# Revit family: F1120-C
name_source: partatom
category: Plumbing Fixtures
revit_build: Autodesk Revit 2018 (Build: 20170223_1515(x64)
units: mm (PartAtom-declared; Revit-internal decimal feet)

## family parameters
Cut with Voids When Loaded = No
Host = Face
Part Type = Normal
Room Calculation Point = No
Round Connector Dimension = Use Radius
Shared = No

## types (3) — shared parameters
Default Elevation = 0' - 0"
Description = FLOOR DRAIN WITH INTEGRAL DEEP SEAL TRAP
Floor Drain Material = Paint - Sherwin Williams Paint - #952C2A - Bellwood Red
Manufacturer = MIFAB
Model = F1120-C
URL = WWW.MIFAB.COM
zero-valued in all types: CWFU, WFU

## per-type parameters (varying)
| type | A | Adjustment | B | Free Area | Pipe Diameter | Pipe Radius | Top Diameter |
| F1120-C - Ø2" | 0' - 2 1/4" | 0' - 1 1/2" | 0' - 5 3/16" | 0' - 8" | 0' - 2" | 0' - 1" | 0' - 5" |
| F1120-C - Ø3" | 0' - 2 1/2" | 0' - 1 1/2" | 0' - 5 3/16" | 0' - 9" | 0' - 3" | 0' - 1 1/2" | 0' - 6" |
| F1120-C - Ø4" | 0' - 2 3/4" | 0' - 1 9/16" | 0' - 7 3/8" | 0' - 10" | 0' - 4" | 0' - 2" | 0' - 7" |

## geometry (parser evidence)
native form markers: Sweep x10
no freeform markers — native parametric forms only
